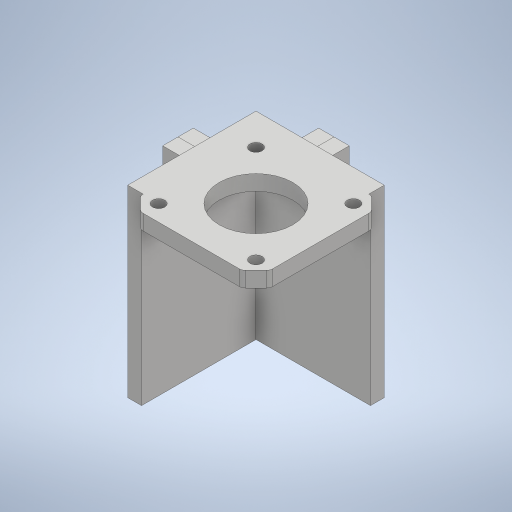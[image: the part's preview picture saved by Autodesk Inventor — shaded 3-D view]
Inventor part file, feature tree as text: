
AUTODESK INVENTOR PART (.ipt)
format: ipt  version: 2023 (Build 270158000, 158)  size: 437,248 bytes
history: native  units: mm
features: extrude x9, sketch x8, projected_geometry x4, other x3, fillet x1, reference x1
ambient origin geometry x8: Origin, YZ Plane, XZ Plane, XY Plane, X Axis, Y Axis, Z Axis, Center Point
bodies: Solid1 (feature_tree)
feature tree (26):
  extrude  "Extrusion1"  Depth=4.0mm
  extrude  "Extrusion3"  Depth=4.0mm
  extrude  "Extrusion4"  Depth=5.0mm TaperAngle=0.0deg
  extrude  "Extrusion9"  Depth=5.0mm
  extrude  "Extrusion7"  Depth=5.0mm TaperAngle=0.0deg
  extrude  "Extrusion10"  Depth=0.5mm
  extrude  "Extrusion11"  Depth=20.0mm TaperAngle=0.0deg
  extrude  "Extrusion12"  Depth=5.0mm
  fillet  "Fillet1"  Radius=4.5mm
  extrude  "Extrusion13"  Depth=0.5mm
  sketch  "Sketch1"  dims[d0=24.0mm d1=4.0mm]
  reference  "Reference1"
  sketch  "Sketch4"  dims[d2=4.0mm d3=4.0mm]
  projected_geometry  "Projected Loop1"
  sketch  "Sketch7"  dims[d4=4.0mm d5=5.0mm d6=0.0mm]
  sketch  "Sketch11"  dims[d11=5.0mm d12=5.0mm]
  sketch  "Sketch12"  dims[d15=40.0mm d16=0.0mm d17=5.0mm d18=0.0mm]
  sketch  "Sketch13"  dims[d35=0.5mm d36=0.5mm]
  sketch  "Sketch14"  dims[d37=35.0mm d38=0.0mm d52=20.0mm d53=0.0mm]
  projected_geometry  "Projected Loop2"
  sketch  "Sketch15"  dims[d54=5.0mm d55=5.0mm d56=4.5mm d57=0.5mm d58=20.0mm d59=0.0mm d60=10.0mm d61=10.0mm d62=5.0mm d63=5.0mm d64=20.0mm d65=10.0mm d66=20.0mm d67=0.0mm d68=10.0mm d69=10.0mm d70=20.0mm d71=10.0mm d72=5.0mm d73=5.0mm d74=40.0mm d75=0.0mm d76=5.0mm d77=8.0mm d78=8.0mm d79=5.0mm d80=5.0mm d81=20.0mm d82=20.0mm d83=0.0mm d84=0.0mm d85=20.0mm d86=0.0mm]
  projected_geometry  "Projected Loop3"
  projected_geometry  "Projected Loop4"
  other  "<userpath>\OneDrive\ClawdDrive\Objet3D\3DPrinter\inventor\3DPrinterBeltCoreXY.iam"
  other  "3DPrinterBeltCoreXY.iam"
  other  "E3D Stepper Motor:1"
